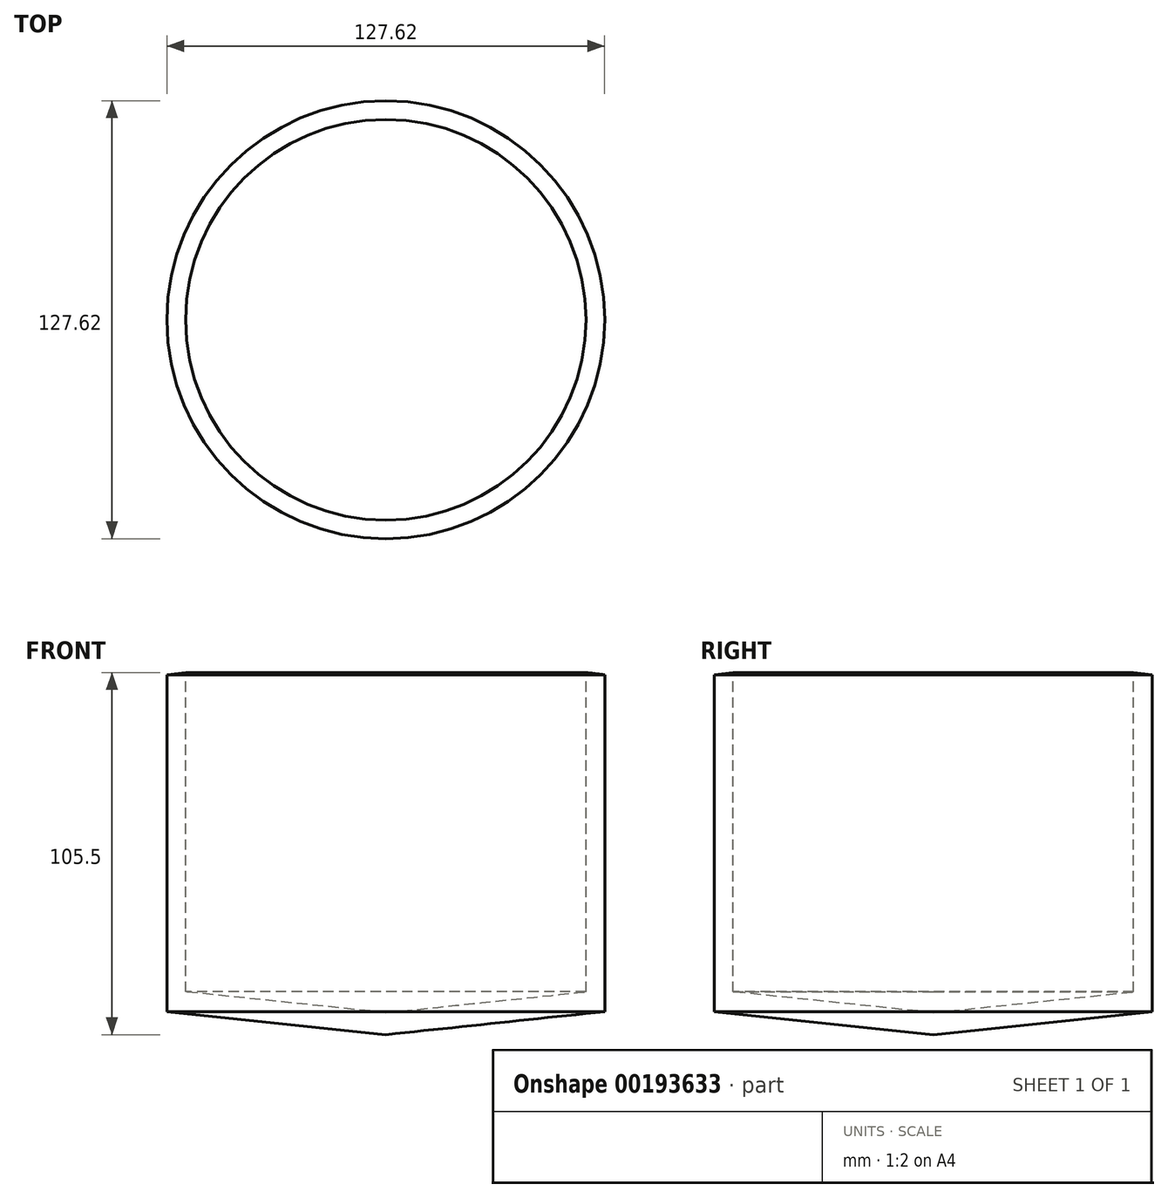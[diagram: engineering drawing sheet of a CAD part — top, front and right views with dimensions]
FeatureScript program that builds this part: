
annotation { "Feature Type Name" : "Feature", "Feature Type Description" : "" }
export const myFeature = defineFeature(function(context is Context, id is Id, definition is map)
    precondition{}
    {
        {
            var Q0;
            Q0=qCreatedBy(makeId("Front.planeOp"),FACE);
            var sketch = newSketch(context, id + "F0", { "sketchPlane" : qUnion([Q0])});
            skLineSegment(sketch, "E0", {"start": v(0, 62.37) * mm, "end": v(0, -49.86) * mm});
            skLineSegment(sketch, "E1", {"start": v(58.36, 55.64) * mm, "end": v(58.36, -37.36) * mm});
            skLineSegment(sketch, "E2", {"start": v(58.36, -37.36) * mm, "end": v(0, -43.45) * mm});
            skLineSegment(sketch, "E3", {"start": v(0, -49.86) * mm, "end": v(63.81, -43.13) * mm});
            skLineSegment(sketch, "E4", {"start": v(63.81, -43.13) * mm, "end": v(63.81, 55) * mm});
            skLineSegment(sketch, "E5", {"start": v(58.36, 55.64) * mm, "end": v(63.81, 55) * mm});
            skSolve(sketch);
        }
        {
            var Q0;
            Q0=makeQuery(id+"F0.imprint","IMPRINT",FACE,{"disambiguationData":[TD([[makeQuery(id+"F0.imprint","IMPRINT",EDGE,{"derivedFrom":sQuery(id+"F0.wireOp",EDGE,"E1")}),1.0]])]});
            var Q1;
            Q1=sQuery(id+"F0.wireOp",EDGE,"E0");
            revolve(context, id + "F1", {"entities" : qUnion([Q0]), "axis" : qUnion([Q1]), "revolveType" : RevolveType.FULL});
        }
    });
